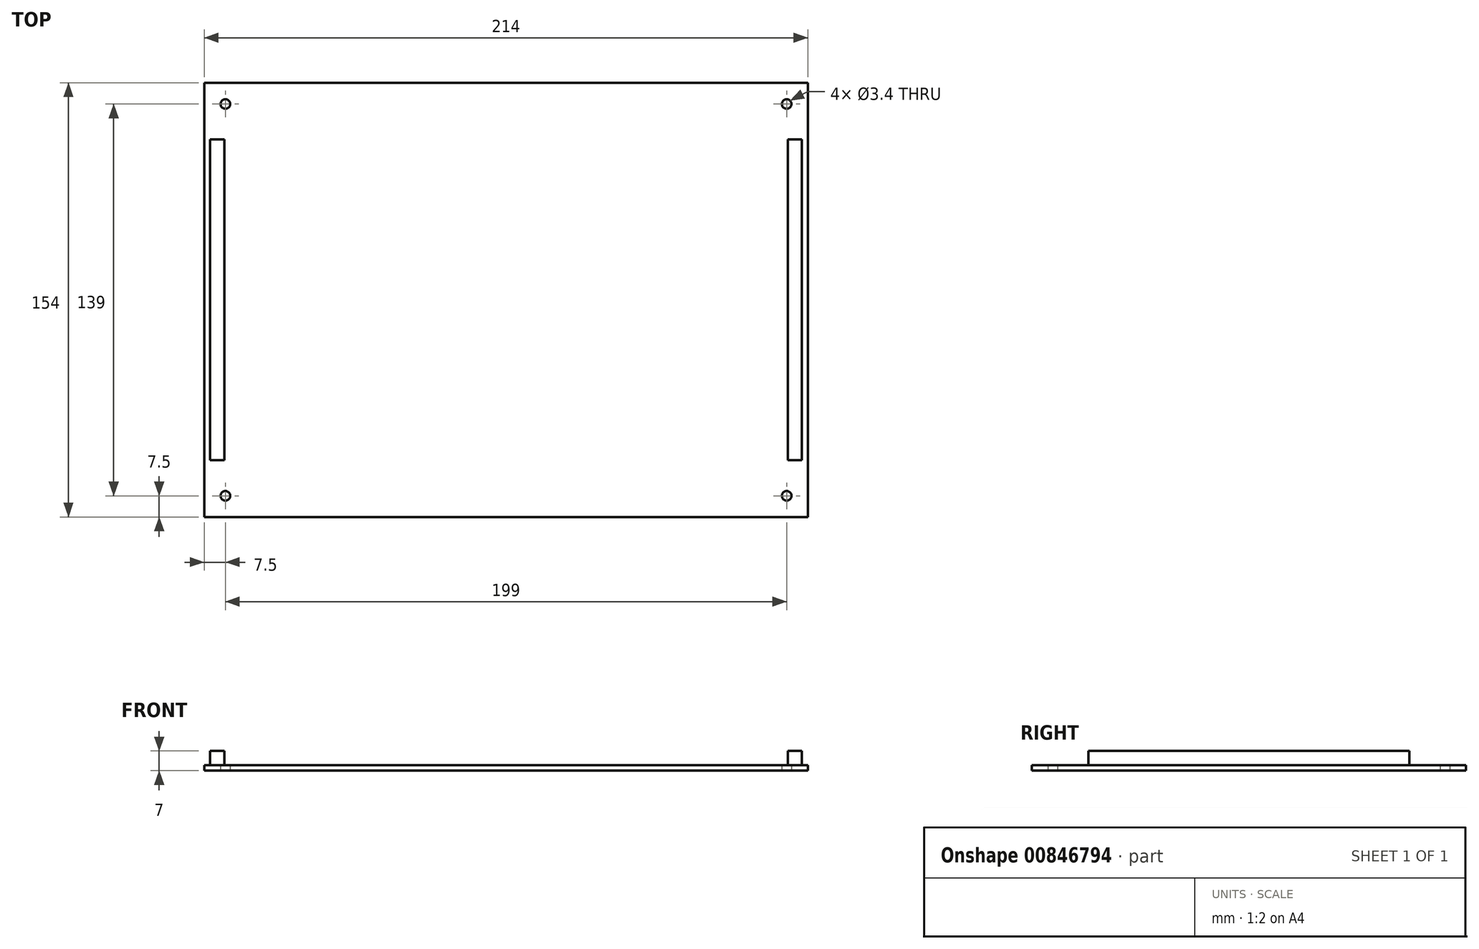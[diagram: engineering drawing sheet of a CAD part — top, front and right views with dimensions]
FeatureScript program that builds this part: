
annotation { "Feature Type Name" : "Feature", "Feature Type Description" : "" }
export const myFeature = defineFeature(function(context is Context, id is Id, definition is map)
    precondition{}
    {
        {
            var Q0;
            Q0=qCreatedBy(makeId("Top.planeOp"),FACE);
            var sketch = newSketch(context, id + "F0", { "sketchPlane" : qUnion([Q0])});
            skLineSegment(sketch, "E0.bottom", {"start": v(107, 77) * mm, "end": v(-107, 77) * mm});
            skLineSegment(sketch, "E0.top", {"start": v(107, -77) * mm, "end": v(-107, -77) * mm});
            skLineSegment(sketch, "E0.left", {"start": v(107, 77) * mm, "end": v(107, -77) * mm});
            skLineSegment(sketch, "E0.right", {"start": v(-107, 77) * mm, "end": v(-107, -77) * mm});
            skPoint(sketch, "E0.middle", {"position": v(0, 0) * mm});
            skPoint(sketch, "E1", {"position": v(-107, -81) * mm});
            skPoint(sketch, "E2", {"position": v(-111, -77) * mm});
            skPoint(sketch, "E3", {"position": v(-111, -81) * mm});
            skPoint(sketch, "E4", {"position": v(-111, 81) * mm});
            skPoint(sketch, "E5", {"position": v(-111, 77) * mm});
            skPoint(sketch, "E6", {"position": v(-107, 81) * mm});
            skPoint(sketch, "E7", {"position": v(111, -81) * mm});
            skPoint(sketch, "E8", {"position": v(111, 81) * mm});
            skPoint(sketch, "E9", {"position": v(111, -77) * mm});
            skPoint(sketch, "E10", {"position": v(111, 77) * mm});
            skPoint(sketch, "E11", {"position": v(-102, -72) * mm});
            skPoint(sketch, "E12", {"position": v(-102, 72) * mm});
            skPoint(sketch, "E13", {"position": v(102, 72) * mm});
            skPoint(sketch, "E14", {"position": v(102, -72) * mm});
            skSolve(sketch);
        }
        {
            var Q0;
            {var subQ5=sQuery(id+"F0.wireOp",EDGE,"W1KJlTXh-5bAP-AzHk-uIRl-KUT3LDjBzCP6");var subQ13=sQuery(id+"F0.wireOp",EDGE,"E0.bottom");var subQ14=makeQuery(id+"F0.imprint","INTERSECT",VERTEX,{"derivedFrom":[subQ13,subQ5]});Q0=makeQuery(id+"F0.imprint","IMPRINT",FACE,{"disambiguationData":[TD([[makeQuery(id+"F0.imprint","IMPRINT",EDGE,{"disambiguationData":[TD([[subQ14,-1.0]])],"derivedFrom":subQ13}),1.0]])]});}
            var Q1;
            {var subQ0=sQuery(id+"F0.wireOp",EDGE,"E0.right");var subQ1=sQuery(id+"F0.wireOp",EDGE,"E0.bottom");var subQ2=makeQuery(id+"F0.imprint","INTERSECT",VERTEX,{"derivedFrom":[subQ1,subQ0]});Q1=makeQuery(id+"F0.imprint","IMPRINT",FACE,{"disambiguationData":[TD([[makeQuery(id+"F0.imprint","IMPRINT",EDGE,{"disambiguationData":[TD([[subQ2,1.0]])],"derivedFrom":subQ1}),1.0]])]});}
            var Q2;
            {var subQ0=sQuery(id+"F0.wireOp",EDGE,"E0.right");var subQ1=sQuery(id+"F0.wireOp",EDGE,"E0.bottom");var subQ2=makeQuery(id+"F0.imprint","INTERSECT",VERTEX,{"derivedFrom":[subQ1,subQ0]});Q2=makeQuery(id+"F0.imprint","IMPRINT",FACE,{"disambiguationData":[TD([[makeQuery(id+"F0.imprint","IMPRINT",EDGE,{"disambiguationData":[TD([[subQ2,1.0]])],"derivedFrom":subQ1}),-1.0]])]});}
            var Q3;
            {var subQ0=sQuery(id+"F0.wireOp",EDGE,"E0.left");var subQ1=sQuery(id+"F0.wireOp",EDGE,"E0.bottom");var subQ2=makeQuery(id+"F0.imprint","INTERSECT",VERTEX,{"derivedFrom":[subQ1,subQ0]});Q3=makeQuery(id+"F0.imprint","IMPRINT",FACE,{"disambiguationData":[TD([[makeQuery(id+"F0.imprint","IMPRINT",EDGE,{"disambiguationData":[TD([[subQ2,-1.0]])],"derivedFrom":subQ1}),1.0]])]});}
            var Q4;
            {var subQ0=sQuery(id+"F0.wireOp",EDGE,"E0.left");var subQ1=sQuery(id+"F0.wireOp",EDGE,"E0.bottom");var subQ2=makeQuery(id+"F0.imprint","INTERSECT",VERTEX,{"derivedFrom":[subQ1,subQ0]});Q4=makeQuery(id+"F0.imprint","IMPRINT",FACE,{"disambiguationData":[TD([[makeQuery(id+"F0.imprint","IMPRINT",EDGE,{"disambiguationData":[TD([[subQ2,-1.0]])],"derivedFrom":subQ1}),-1.0]])]});}
            var Q5;
            {var subQ0=sQuery(id+"F0.wireOp",EDGE,"E0.left");var subQ1=sQuery(id+"F0.wireOp",EDGE,"E0.top");var subQ2=makeQuery(id+"F0.imprint","INTERSECT",VERTEX,{"derivedFrom":[subQ1,subQ0]});Q5=makeQuery(id+"F0.imprint","IMPRINT",FACE,{"disambiguationData":[TD([[makeQuery(id+"F0.imprint","IMPRINT",EDGE,{"disambiguationData":[TD([[subQ2,-1.0]])],"derivedFrom":subQ1}),-1.0]])]});}
            var Q6;
            {var subQ0=sQuery(id+"F0.wireOp",EDGE,"E0.left");var subQ1=sQuery(id+"F0.wireOp",EDGE,"E0.top");var subQ2=makeQuery(id+"F0.imprint","INTERSECT",VERTEX,{"derivedFrom":[subQ1,subQ0]});Q6=makeQuery(id+"F0.imprint","IMPRINT",FACE,{"disambiguationData":[TD([[makeQuery(id+"F0.imprint","IMPRINT",EDGE,{"disambiguationData":[TD([[subQ2,-1.0]])],"derivedFrom":subQ1}),1.0]])]});}
            var Q7;
            {var subQ0=sQuery(id+"F0.wireOp",EDGE,"E0.right");var subQ1=sQuery(id+"F0.wireOp",EDGE,"E0.top");var subQ2=makeQuery(id+"F0.imprint","INTERSECT",VERTEX,{"derivedFrom":[subQ1,subQ0]});Q7=makeQuery(id+"F0.imprint","IMPRINT",FACE,{"disambiguationData":[TD([[makeQuery(id+"F0.imprint","IMPRINT",EDGE,{"disambiguationData":[TD([[subQ2,1.0]])],"derivedFrom":subQ1}),-1.0]])]});}
            var Q8;
            {var subQ0=sQuery(id+"F0.wireOp",EDGE,"E0.right");var subQ1=sQuery(id+"F0.wireOp",EDGE,"E0.top");var subQ2=makeQuery(id+"F0.imprint","INTERSECT",VERTEX,{"derivedFrom":[subQ1,subQ0]});Q8=makeQuery(id+"F0.imprint","IMPRINT",FACE,{"disambiguationData":[TD([[makeQuery(id+"F0.imprint","IMPRINT",EDGE,{"disambiguationData":[TD([[subQ2,1.0]])],"derivedFrom":subQ1}),1.0]])]});}
            extrude(context, id + "F1", {"entities" : qUnion([Q0, Q1, Q2, Q3, Q4, Q5, Q6, Q7, Q8]), "depth" : 2 * mm, "offsetDistance" : 25 * mm});
        }
        {
            var Q0;
            Q0=makeQuery(id+"F1.opExtrude","CAP_FACE",FACE,{"disambiguationData":[OSD([sQuery(id+"F0.wireOp",EDGE,"E0.bottom"),sQuery(id+"F0.wireOp",EDGE,"E0.top"),sQuery(id+"F0.wireOp",EDGE,"E0.left"),sQuery(id+"F0.wireOp",EDGE,"E0.right")])],"isStart":false});
            var sketch = newSketch(context, id + "F2", { "sketchPlane" : qUnion([Q0])});
            skLineSegment(sketch, "E15.bottom", {"start": v(104.9, -74.9) * mm, "end": v(-104.9, -74.9) * mm});
            skLineSegment(sketch, "E15.top", {"start": v(104.9, 74.9) * mm, "end": v(-104.9, 74.9) * mm});
            skLineSegment(sketch, "E15.left", {"start": v(104.9, -74.9) * mm, "end": v(104.9, 74.9) * mm});
            skLineSegment(sketch, "E15.right", {"start": v(-104.9, -74.9) * mm, "end": v(-104.9, 74.9) * mm});
            skPoint(sketch, "E15.middle", {"position": v(0, 0) * mm});
            skCircle(sketch, "E16", {"center": v(-104.9, 74.9) * mm, "radius": 17.5 * mm});
            skCircle(sketch, "E17", {"center": v(104.9, 74.9) * mm, "radius": 17.5 * mm});
            skCircle(sketch, "E18", {"center": v(104.9, -74.9) * mm, "radius": 17.5 * mm});
            skCircle(sketch, "E19", {"center": v(-104.9, -74.9) * mm, "radius": 17.5 * mm});
            skLineSegment(sketch, "E20.bottom", {"start": v(-86.9, 74.9) * mm, "end": v(86.9, 74.9) * mm});
            skLineSegment(sketch, "E20.top", {"start": v(-86.9, 69.9) * mm, "end": v(86.9, 69.9) * mm});
            skLineSegment(sketch, "E20.left", {"start": v(-86.9, 74.9) * mm, "end": v(-86.9, 69.9) * mm});
            skLineSegment(sketch, "E20.right", {"start": v(86.9, 74.9) * mm, "end": v(86.9, 69.9) * mm});
            skLineSegment(sketch, "E21.bottom", {"start": v(-104.9, 56.9) * mm, "end": v(-99.9, 56.9) * mm});
            skLineSegment(sketch, "E21.top", {"start": v(-104.9, -56.9) * mm, "end": v(-99.9, -56.9) * mm});
            skLineSegment(sketch, "E21.left", {"start": v(-104.9, 56.9) * mm, "end": v(-104.9, -56.9) * mm});
            skLineSegment(sketch, "E21.right", {"start": v(-99.9, 56.9) * mm, "end": v(-99.9, -56.9) * mm});
            skLineSegment(sketch, "E22.bottom", {"start": v(-86.9, -74.9) * mm, "end": v(86.9, -74.9) * mm});
            skLineSegment(sketch, "E22.top", {"start": v(-86.9, -69.9) * mm, "end": v(86.9, -69.9) * mm});
            skLineSegment(sketch, "E22.left", {"start": v(-86.9, -74.9) * mm, "end": v(-86.9, -69.9) * mm});
            skLineSegment(sketch, "E22.right", {"start": v(86.9, -74.9) * mm, "end": v(86.9, -69.9) * mm});
            skLineSegment(sketch, "E23.bottom", {"start": v(104.9, -56.9) * mm, "end": v(99.9, -56.9) * mm});
            skLineSegment(sketch, "E23.top", {"start": v(104.9, 56.9) * mm, "end": v(99.9, 56.9) * mm});
            skLineSegment(sketch, "E23.left", {"start": v(104.9, -56.9) * mm, "end": v(104.9, 56.9) * mm});
            skLineSegment(sketch, "E23.right", {"start": v(99.9, -56.9) * mm, "end": v(99.9, 56.9) * mm});
            skSolve(sketch);
        }
        {
            var Q0;
            Q0=makeQuery(id+"F2.imprint","IMPRINT",FACE,{"disambiguationData":[TD([[makeQuery(id+"F2.imprint","IMPRINT",EDGE,{"derivedFrom":sQuery(id+"F2.wireOp",EDGE,"E21.bottom")}),-1.0]])]});
            var Q1;
            Q1=makeQuery(id+"F2.imprint","IMPRINT",FACE,{"disambiguationData":[TD([[makeQuery(id+"F2.imprint","IMPRINT",EDGE,{"derivedFrom":sQuery(id+"F2.wireOp",EDGE,"E20.bottom")}),-1.0]])]});
            var Q2;
            Q2=makeQuery(id+"F2.imprint","IMPRINT",FACE,{"disambiguationData":[TD([[makeQuery(id+"F2.imprint","IMPRINT",EDGE,{"derivedFrom":sQuery(id+"F2.wireOp",EDGE,"E23.bottom")}),-1.0]])]});
            var Q3;
            Q3=makeQuery(id+"F2.imprint","IMPRINT",FACE,{"disambiguationData":[TD([[makeQuery(id+"F2.imprint","IMPRINT",EDGE,{"derivedFrom":sQuery(id+"F2.wireOp",EDGE,"E22.bottom")}),1.0]])]});
            extrude(context, id + "F3", {"entities" : qUnion([Q0, Q1, Q2, Q3]), "operationType" : NewBodyOperationType.ADD, "depth" : 5 * mm, "offsetDistance" : 25 * mm});
        }
        {
            var Q0;
            Q0=makeQuery(id+"F1.opExtrude","CAP_FACE",FACE,{"disambiguationData":[OSD([sQuery(id+"F0.wireOp",EDGE,"E0.bottom"),sQuery(id+"F0.wireOp",EDGE,"E0.top"),sQuery(id+"F0.wireOp",EDGE,"E0.left"),sQuery(id+"F0.wireOp",EDGE,"E0.right")])],"isStart":true});
            var sketch = newSketch(context, id + "F4", { "sketchPlane" : qUnion([Q0])});
            skPoint(sketch, "E24", {"position": v(-99.5, 69.5) * mm});
            skPoint(sketch, "E25", {"position": v(99.5, 69.5) * mm});
            skPoint(sketch, "E26", {"position": v(99.5, -69.5) * mm});
            skPoint(sketch, "E27", {"position": v(-99.5, -69.5) * mm});
            skSolve(sketch);
        }
        {
            var Q0;
            Q0=sQuery(id+"F4.wireOp",VERTEX,"E27");
            var Q1;
            Q1=sQuery(id+"F4.wireOp",VERTEX,"E24");
            var Q2;
            Q2=sQuery(id+"F4.wireOp",VERTEX,"E25");
            var Q3;
            Q3=sQuery(id+"F4.wireOp",VERTEX,"E26");
            var Q4;
            Q4=makeQuery(id+"F1.opExtrude","SWEPT_BODY",BODY,{"disambiguationData":[OSD([sQuery(id+"F0.wireOp",EDGE,"E0.bottom"),sQuery(id+"F0.wireOp",EDGE,"E0.top"),sQuery(id+"F0.wireOp",EDGE,"E0.left"),sQuery(id+"F0.wireOp",EDGE,"E0.right")])]});
            hole(context, id + "F5", {"style" : HoleStyle.SIMPLE, "endStyle" : HoleEndStyle.BLIND, "standardTappedOrClearance" : lookupTablePath({ "fit" : "Normal", "standard" : "ISO", "size" : "M3", "type" : "Clearance" }), "standardBlindInLast" : lookupTablePath({ "fit" : "Normal", "standard" : "ISO", "size" : "M3", "type" : "Clearance" }), "holeDiameter" : 3.4 * mm, "majorDiameter" : 5 * mm, "holeDepth" : 5 * mm, "isTappedThrough" : true, "tappedDepth" : 12 * mm, "tapClearance" : 3, "locations" : qUnion([Q0, Q1, Q2, Q3]), "scope" : qUnion([Q4])});
        }
    });
